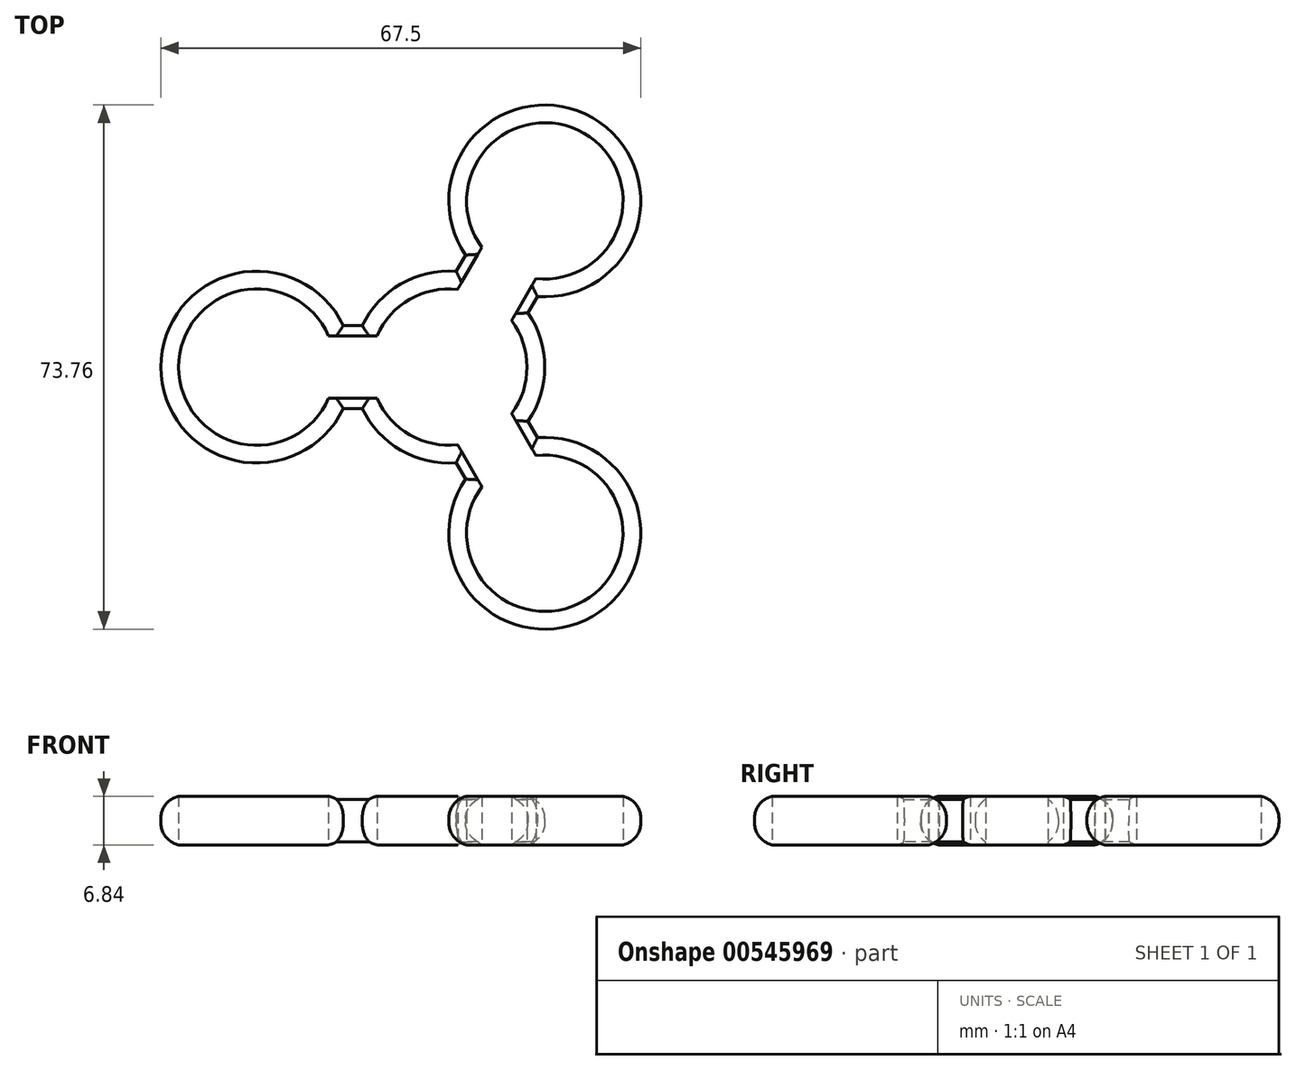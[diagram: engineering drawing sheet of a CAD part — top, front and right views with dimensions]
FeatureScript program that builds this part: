
annotation { "Feature Type Name" : "Feature", "Feature Type Description" : "" }
export const myFeature = defineFeature(function(context is Context, id is Id, definition is map)
    precondition{}
    {
        {
            var Q0;
            Q0=qCreatedBy(makeId("Top.planeOp"),FACE);
            var sketch = newSketch(context, id + "F0", { "sketchPlane" : qUnion([Q0])});
            skPoint(sketch, "E0.0.midPoint", {"position": v(13.5, 0) * mm});
            skCircle(sketch, "E1", {"center": v(0, 0) * mm, "radius": 11 * mm});
            skCircle(sketch, "E2", {"center": v(-27, 0) * mm, "radius": 11 * mm});
            skCircle(sketch, "E3", {"center": v(13.5, 23.38) * mm, "radius": 11 * mm});
            skCircle(sketch, "E4", {"center": v(13.5, -23.38) * mm, "radius": 11 * mm});
            skPoint(sketch, "E5.2.internal.snap0", {"position": v(-6.75, -11.7) * mm});
            skArc(sketch, "E6", {"start": v(-12.17, -5.85) * mm, "mid": v(-6.75, -11.7) * mm, "end": v(1.02, -13.46) * mm});
            skArc(sketch, "E7", {"start": v(2.35, -15.77) * mm, "mid": v(20.25, -35.07) * mm, "end": v(12.48, -9.92) * mm});
            skArc(sketch, "E8", {"start": v(12.48, 9.92) * mm, "mid": v(20.25, 35.07) * mm, "end": v(2.35, 15.77) * mm});
            skArc(sketch, "E9", {"start": v(-14.83, 5.85) * mm, "mid": v(-40.5, 0) * mm, "end": v(-14.83, -5.85) * mm});
            skLineSegment(sketch, "E10", {"start": v(-12.17, -5.85) * mm, "end": v(-14.83, -5.85) * mm});
            skLineSegment(sketch, "E11", {"start": v(-14.83, 5.85) * mm, "end": v(-12.17, 5.85) * mm});
            skLineSegment(sketch, "E12", {"start": v(1.02, -13.46) * mm, "end": v(2.35, -15.77) * mm});
            skLineSegment(sketch, "E13", {"start": v(11.15, -7.62) * mm, "end": v(12.48, -9.92) * mm});
            skLineSegment(sketch, "E14", {"start": v(11.15, 7.62) * mm, "end": v(12.48, 9.92) * mm});
            skLineSegment(sketch, "E15", {"start": v(1.02, 13.46) * mm, "end": v(2.35, 15.77) * mm});
            skPoint(sketch, "E16.orphan", {"position": v(-17.68, 5.85) * mm});
            skPoint(sketch, "E17.orphan", {"position": v(-17.68, -5.85) * mm});
            skArc(sketch, "E18.trimOffspring", {"start": v(11.15, -7.62) * mm, "mid": v(13.5, 0) * mm, "end": v(11.15, 7.62) * mm});
            skArc(sketch, "E19.trimOffspring", {"start": v(1.02, 13.46) * mm, "mid": v(-6.75, 11.7) * mm, "end": v(-12.17, 5.85) * mm});
            skLineSegment(sketch, "E20", {"start": v(12.1, 12.22) * mm, "end": v(10.04, 8.64) * mm});
            skLineSegment(sketch, "E21", {"start": v(4.52, 16.6) * mm, "end": v(2.45, 13.02) * mm});
            skLineSegment(sketch, "E22", {"start": v(-16.64, -4.38) * mm, "end": v(-12.5, -4.38) * mm});
            skLineSegment(sketch, "E23", {"start": v(-16.64, 4.38) * mm, "end": v(-12.5, 4.38) * mm});
            skLineSegment(sketch, "E24", {"start": v(4.53, -16.6) * mm, "end": v(2.46, -13.01) * mm});
            skLineSegment(sketch, "E25", {"start": v(12.12, -12.21) * mm, "end": v(10.05, -8.63) * mm});
            skLineSegment(sketch, "E26", {"start": v(10.04, 8.64) * mm, "end": v(12.25, 12.45) * mm});
            skLineSegment(sketch, "E27", {"start": v(2.45, 13.02) * mm, "end": v(4.65, 16.84) * mm});
            skLineSegment(sketch, "E28", {"start": v(-12.5, -4.38) * mm, "end": v(-16.91, -4.38) * mm});
            skLineSegment(sketch, "E29", {"start": v(-12.5, 4.38) * mm, "end": v(-16.91, 4.38) * mm});
            skLineSegment(sketch, "E30", {"start": v(2.46, -13.01) * mm, "end": v(4.66, -16.83) * mm});
            skLineSegment(sketch, "E31", {"start": v(10.05, -8.63) * mm, "end": v(12.26, -12.45) * mm});
            skLineSegment(sketch, "E32", {"start": v(-12.5, 4.38) * mm, "end": v(-10.09, 4.38) * mm});
            skLineSegment(sketch, "E33", {"start": v(-12.5, -4.38) * mm, "end": v(-10.09, -4.38) * mm});
            skLineSegment(sketch, "E34", {"start": v(2.45, 13.02) * mm, "end": v(1.24, 10.93) * mm});
            skLineSegment(sketch, "E35", {"start": v(10.04, 8.64) * mm, "end": v(8.84, 6.55) * mm});
            skLineSegment(sketch, "E36", {"start": v(10.05, -8.63) * mm, "end": v(8.85, -6.54) * mm});
            skLineSegment(sketch, "E37", {"start": v(2.46, -13.01) * mm, "end": v(1.25, -10.93) * mm});
            skSolve(sketch);
        }
        {
            var Q0;
            Q0 = qSketchRegion(id + "F0", true);
            extrude(context, id + "F1", {"entities" : qUnion([Q0]), "depth" : 7 * mm, "offsetDistance" : 25.4 * mm});
        }
        {
            var Q0;
            Q0=makeQuery(id+"F1.opExtrude","CAP_EDGE",EDGE,{"disambiguationData":[OSD([sQuery(id+"F0.wireOp",EDGE,"E9")])],"isStart":false});
            var Q1;
            Q1=makeQuery(id+"F1.opExtrude","CAP_EDGE",EDGE,{"disambiguationData":[OSD([sQuery(id+"F0.wireOp",EDGE,"E10")])],"isStart":false});
            var Q2;
            Q2=makeQuery(id+"F1.opExtrude","CAP_EDGE",EDGE,{"disambiguationData":[OSD([sQuery(id+"F0.wireOp",EDGE,"E6")])],"isStart":false});
            var Q3;
            Q3=makeQuery(id+"F1.opExtrude","CAP_EDGE",EDGE,{"disambiguationData":[OSD([sQuery(id+"F0.wireOp",EDGE,"E7")])],"isStart":false});
            var Q4;
            Q4=makeQuery(id+"F1.opExtrude","CAP_EDGE",EDGE,{"disambiguationData":[OSD([sQuery(id+"F0.wireOp",EDGE,"E12")])],"isStart":false});
            var Q5;
            Q5=makeQuery(id+"F1.opExtrude","CAP_EDGE",EDGE,{"disambiguationData":[OSD([sQuery(id+"F0.wireOp",EDGE,"E13")])],"isStart":false});
            var Q6;
            Q6=makeQuery(id+"F1.opExtrude","CAP_EDGE",EDGE,{"disambiguationData":[OSD([sQuery(id+"F0.wireOp",EDGE,"E18.trimOffspring")])],"isStart":false});
            var Q7;
            Q7=makeQuery(id+"F1.opExtrude","CAP_EDGE",EDGE,{"disambiguationData":[OSD([sQuery(id+"F0.wireOp",EDGE,"E14")])],"isStart":false});
            var Q8;
            Q8=makeQuery(id+"F1.opExtrude","CAP_EDGE",EDGE,{"disambiguationData":[OSD([sQuery(id+"F0.wireOp",EDGE,"E8")])],"isStart":false});
            var Q9;
            Q9=makeQuery(id+"F1.opExtrude","CAP_EDGE",EDGE,{"disambiguationData":[OSD([sQuery(id+"F0.wireOp",EDGE,"E19.trimOffspring")])],"isStart":false});
            var Q10;
            Q10=makeQuery(id+"F1.opExtrude","CAP_EDGE",EDGE,{"disambiguationData":[OSD([sQuery(id+"F0.wireOp",EDGE,"E11")])],"isStart":false});
            var Q11;
            Q11=makeQuery(id+"F1.opExtrude","CAP_EDGE",EDGE,{"disambiguationData":[OSD([sQuery(id+"F0.wireOp",EDGE,"E15")])],"isStart":false});
            fillet(context, id + "F2", {"entities" : qUnion([Q0, Q1, Q2, Q3, Q4, Q5, Q6, Q7, Q8, Q9, Q10, Q11]), "radius" : 3.2 * mm, "tangentPropagation" : true, "allowEdgeOverflow" : false});
        }
        {
            var Q0;
            Q0=makeQuery(id+"F1.opExtrude","CAP_EDGE",EDGE,{"disambiguationData":[OSD([sQuery(id+"F0.wireOp",EDGE,"E9")])],"isStart":true});
            var Q1;
            Q1=makeQuery(id+"F1.opExtrude","CAP_EDGE",EDGE,{"disambiguationData":[OSD([sQuery(id+"F0.wireOp",EDGE,"E19.trimOffspring")])],"isStart":true});
            var Q2;
            Q2=makeQuery(id+"F1.opExtrude","CAP_EDGE",EDGE,{"disambiguationData":[OSD([sQuery(id+"F0.wireOp",EDGE,"E11")])],"isStart":true});
            var Q3;
            Q3=makeQuery(id+"F1.opExtrude","CAP_EDGE",EDGE,{"disambiguationData":[OSD([sQuery(id+"F0.wireOp",EDGE,"E15")])],"isStart":true});
            var Q4;
            Q4=makeQuery(id+"F1.opExtrude","CAP_EDGE",EDGE,{"disambiguationData":[OSD([sQuery(id+"F0.wireOp",EDGE,"E8")])],"isStart":true});
            var Q5;
            Q5=makeQuery(id+"F1.opExtrude","CAP_EDGE",EDGE,{"disambiguationData":[OSD([sQuery(id+"F0.wireOp",EDGE,"E14")])],"isStart":true});
            var Q6;
            Q6=makeQuery(id+"F1.opExtrude","CAP_EDGE",EDGE,{"disambiguationData":[OSD([sQuery(id+"F0.wireOp",EDGE,"E18.trimOffspring")])],"isStart":true});
            var Q7;
            Q7=makeQuery(id+"F1.opExtrude","CAP_EDGE",EDGE,{"disambiguationData":[OSD([sQuery(id+"F0.wireOp",EDGE,"E13")])],"isStart":true});
            var Q8;
            Q8=makeQuery(id+"F1.opExtrude","CAP_EDGE",EDGE,{"disambiguationData":[OSD([sQuery(id+"F0.wireOp",EDGE,"E7")])],"isStart":true});
            var Q9;
            Q9=makeQuery(id+"F1.opExtrude","CAP_EDGE",EDGE,{"disambiguationData":[OSD([sQuery(id+"F0.wireOp",EDGE,"E10")])],"isStart":true});
            var Q10;
            Q10=makeQuery(id+"F1.opExtrude","CAP_EDGE",EDGE,{"disambiguationData":[OSD([sQuery(id+"F0.wireOp",EDGE,"E6")])],"isStart":true});
            var Q11;
            Q11=makeQuery(id+"F1.opExtrude","CAP_EDGE",EDGE,{"disambiguationData":[OSD([sQuery(id+"F0.wireOp",EDGE,"E12")])],"isStart":true});
            fillet(context, id + "F3", {"entities" : qUnion([Q0, Q1, Q2, Q3, Q4, Q5, Q6, Q7, Q8, Q9, Q10, Q11]), "radius" : 3.2 * mm, "tangentPropagation" : true, "allowEdgeOverflow" : false});
        }
    });
